# Revit family: HL_RU_Roof drain_HL64.1BF-B-221103
name_source: partatom
category: Instalační zařizovací předměty
units: mm (PartAtom-declared; Revit-internal decimal feet)

## family parameters
Bod výpočtu místnosti = Ano
Kóta kulaté spojky = Použít průměr
Nadpis OmniClass = Deck Waste Water Drains
Ořezat dutým tvarem při načtení = Ne
Sdílené = Ne
Typ dílu = Normální
Vždy vertikální = Ano
Založené na pracovní rovině = Ne
Číslo OmniClass = 23.70.50.21.24.14

## types (2) — shared parameters
Popis = Кровельные воронки
Přípoj CW = Ne
Přípoj HW = Ne
Přípoj odpadních dílů = Ano
Přípoj ventilace = Ne
URL = http://www.hutterer-lechner.com
Výrobce = HL Hutterer & Lechner GmbH
МАКСИМАЛЬНАЯ НАГРУЗКА КЛАССА = K - 300 kg
МАТЕРИАЛ = PP
НАСАДКА = 19-65mm/148x148mm
ПРОИЗВОДИТЕЛЬНОСТЬ = 3,7 l/s
РЕШЁТКА = Edelstahl 137x137mm
zero-valued in all types: Výchozí výška

## per-type parameters (varying)
| type | EAN | Indexovaná poznámka | Komentáře k typům | Model | ВЕС | НОМИНАЛЬНЫЙ ДИАМЕТР | РАЗМЕР |
| HL_Кровельная воронка_HL64.1BF_1 | 9003076031580 | HL64.1BF_1 | HL64.1BF/1 Кровельная воронка DN110 для эксплуатируемой кровли, горизонтальный выпуск, с ПП_фланцем и электрообогревом (10_30W/230V), | HL64.1BF_1 | 1,18 [kg] | 110 mm | DN110 |
| HL_Кровельная воронка_HL64.1BF_7 | 9003076031566 | HL64.1BF_7 | HL64.1BF/7 Кровельная воронка DN75 для эксплуатируемой кровли, горизонтальный выпуск, с ПП_фланцем и электрообогревом (10_30W/230V), | HL64.1BF_7 | 1,16 [kg] | 75 mm | DN75 |

## geometry (parser evidence)
native form markers: Sweep x8
no freeform markers — native parametric forms only
